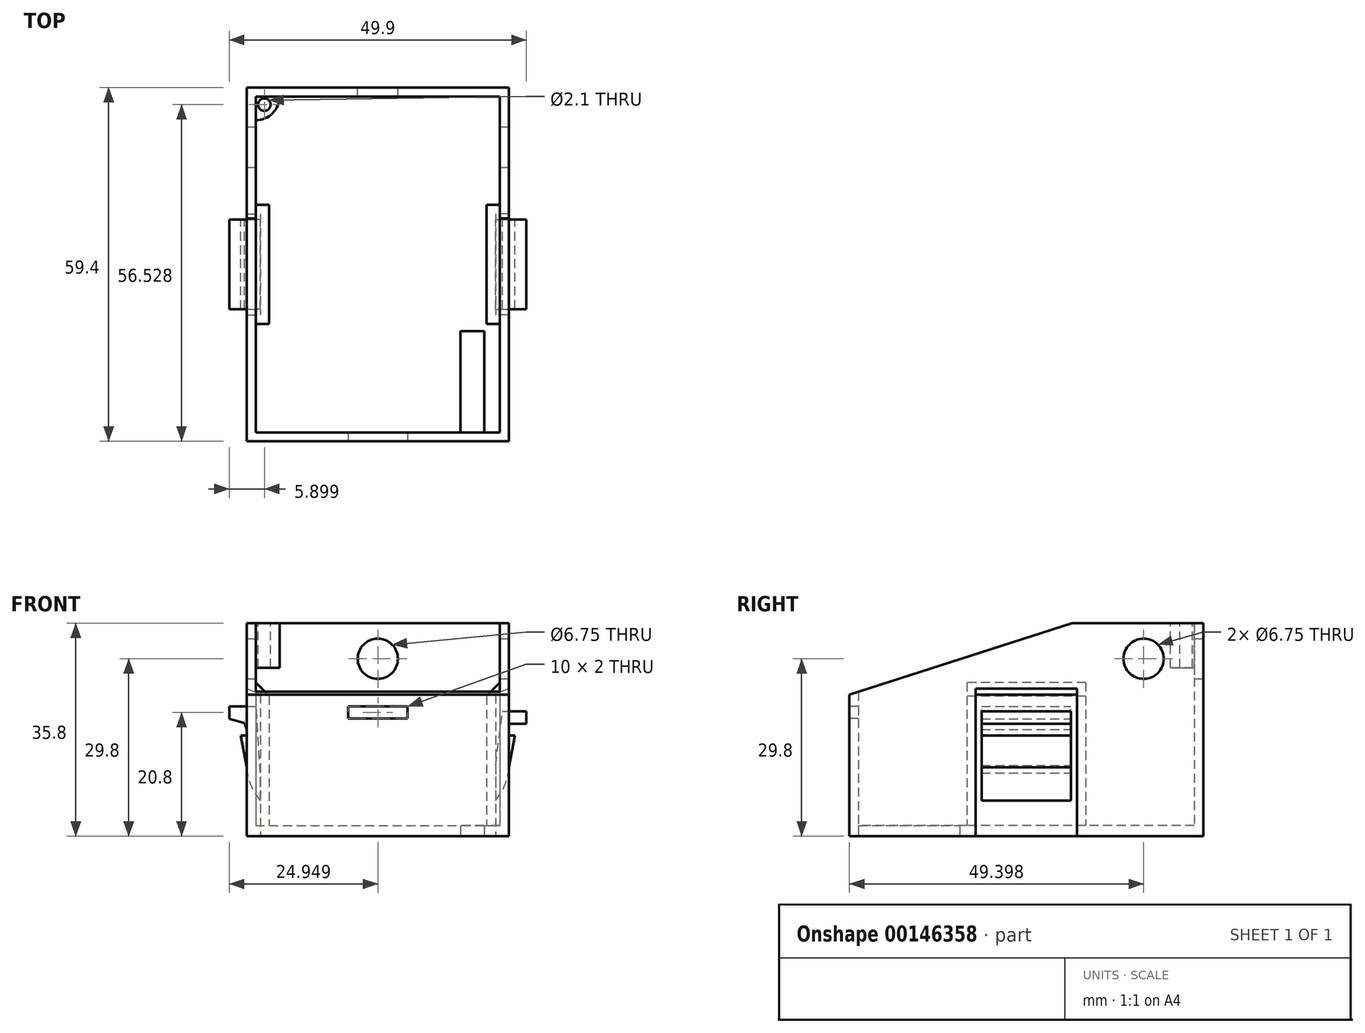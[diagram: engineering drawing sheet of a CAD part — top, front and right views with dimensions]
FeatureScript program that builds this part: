
annotation { "Feature Type Name" : "Feature", "Feature Type Description" : "" }
export const myFeature = defineFeature(function(context is Context, id is Id, definition is map)
    precondition{}
    {
        {
            var Q0;
            Q0=qCreatedBy(makeId("Top.planeOp"),FACE);
            var sketch = newSketch(context, id + "F0", { "sketchPlane" : qUnion([Q0])});
            skLineSegment(sketch, "E0.bottom", {"start": v(-56.63, 54.28) * mm, "end": v(-12.63, 54.28) * mm});
            skLineSegment(sketch, "E0.top", {"start": v(-56.63, -5.12) * mm, "end": v(-12.63, -5.12) * mm});
            skCircle(sketch, "E1", {"center": v(-12.63, -5.12) * mm, "radius": 1.5 * mm, "construction": true});
            skCircle(sketch, "E2", {"center": v(-56.63, -5.12) * mm, "radius": 1.5 * mm, "construction": true});
            skLineSegment(sketch, "E3", {"start": v(-56.63, -3.62) * mm, "end": v(-12.63, -3.62) * mm, "construction": true});
            skCircle(sketch, "E4", {"center": v(-12.63, -3.62) * mm, "radius": 4.1 * mm, "construction": true});
            skLineSegment(sketch, "E5.bottom", {"start": v(-16.73, -3.62) * mm, "end": v(-20.73, -3.62) * mm});
            skLineSegment(sketch, "E5.top", {"start": v(-16.73, 13.38) * mm, "end": v(-20.73, 13.38) * mm});
            skLineSegment(sketch, "E5.left", {"start": v(-16.73, -3.62) * mm, "end": v(-16.73, 13.38) * mm});
            skLineSegment(sketch, "E5.right", {"start": v(-20.73, -3.62) * mm, "end": v(-20.73, 13.38) * mm});
            skLineSegment(sketch, "E6", {"start": v(-56.63, 24.58) * mm, "end": v(-12.63, 24.58) * mm, "construction": true});
            skCircle(sketch, "E7", {"center": v(-56.63, 24.58) * mm, "radius": 8.5 * mm, "construction": true});
            skLineSegment(sketch, "E8", {"start": v(-56.63, 33.08) * mm, "end": v(-54.38, 33.08) * mm});
            skLineSegment(sketch, "E9", {"start": v(-56.63, 16.08) * mm, "end": v(-54.38, 16.08) * mm});
            skLineSegment(sketch, "E10", {"start": v(-54.38, 33.08) * mm, "end": v(-54.38, 16.08) * mm});
            skLineSegment(sketch, "E11", {"start": v(-56.63, 54.28) * mm, "end": v(-56.63, 33.08) * mm});
            skLineSegment(sketch, "E12", {"start": v(-56.63, 16.08) * mm, "end": v(-56.63, -5.12) * mm});
            skLineSegment(sketch, "E13", {"start": v(-34.63, 54.28) * mm, "end": v(-34.63, 40.65) * mm, "construction": true});
            skLineSegment(sketch, "E14.MirrorCS", {"start": v(-12.63, 16.08) * mm, "end": v(-12.63, -5.12) * mm});
            skLineSegment(sketch, "E15.MirrorCS", {"start": v(-12.63, 16.08) * mm, "end": v(-14.88, 16.08) * mm});
            skLineSegment(sketch, "E16.MirrorCS", {"start": v(-12.63, 33.08) * mm, "end": v(-14.88, 33.08) * mm});
            skLineSegment(sketch, "E17.MirrorCS", {"start": v(-12.63, 54.28) * mm, "end": v(-12.63, 33.08) * mm});
            skLineSegment(sketch, "E18.MirrorCS", {"start": v(-14.88, 33.08) * mm, "end": v(-14.88, 16.08) * mm});
            skSolve(sketch);
        }
        {
            var Q0;
            Q0=makeQuery(id+"F0.imprint","IMPRINT",FACE,{"disambiguationData":[TD([[makeQuery(id+"F0.imprint","IMPRINT",EDGE,{"derivedFrom":sQuery(id+"F0.wireOp",EDGE,"E0.bottom")}),-1.0]])]});
            extrude(context, id + "F1", {"entities" : qUnion([Q0]), "depth" : 1.8 * mm});
        }
        {
            var Q0;
            Q0=makeQuery(id+"F1.opExtrude","CAP_FACE",FACE,{"disambiguationData":[OSD([sQuery(id+"F0.wireOp",EDGE,"E0.bottom"),sQuery(id+"F0.wireOp",EDGE,"E0.top"),sQuery(id+"F0.wireOp",EDGE,"E5.bottom"),sQuery(id+"F0.wireOp",EDGE,"E5.top"),sQuery(id+"F0.wireOp",EDGE,"E5.left"),sQuery(id+"F0.wireOp",EDGE,"E5.right"),sQuery(id+"F0.wireOp",EDGE,"E8"),sQuery(id+"F0.wireOp",EDGE,"E9"),sQuery(id+"F0.wireOp",EDGE,"E10"),sQuery(id+"F0.wireOp",EDGE,"E11"),sQuery(id+"F0.wireOp",EDGE,"E12"),sQuery(id+"F0.wireOp",EDGE,"E14.MirrorCS"),sQuery(id+"F0.wireOp",EDGE,"E15.MirrorCS"),sQuery(id+"F0.wireOp",EDGE,"E16.MirrorCS"),sQuery(id+"F0.wireOp",EDGE,"E17.MirrorCS"),sQuery(id+"F0.wireOp",EDGE,"E18.MirrorCS")])],"isStart":false});
            var sketch = newSketch(context, id + "F2", { "sketchPlane" : qUnion([Q0])});
            skLineSegment(sketch, "E19.0", {"start": v(-55.13, 52.78) * mm, "end": v(-55.13, 34.58) * mm});
            skLineSegment(sketch, "E19.1", {"start": v(-14.13, 14.58) * mm, "end": v(-16.38, 14.58) * mm});
            skLineSegment(sketch, "E19.2", {"start": v(-16.38, 34.58) * mm, "end": v(-16.38, 14.58) * mm});
            skLineSegment(sketch, "E19.3", {"start": v(-14.13, 34.58) * mm, "end": v(-16.38, 34.58) * mm});
            skLineSegment(sketch, "E19.4", {"start": v(-14.13, 52.78) * mm, "end": v(-14.13, 34.58) * mm});
            skLineSegment(sketch, "E19.5", {"start": v(-14.13, 14.58) * mm, "end": v(-14.13, -3.62) * mm});
            skLineSegment(sketch, "E19.6", {"start": v(-55.13, 52.78) * mm, "end": v(-14.13, 52.78) * mm});
            skLineSegment(sketch, "E19.7", {"start": v(-55.13, -3.62) * mm, "end": v(-14.13, -3.62) * mm});
            skLineSegment(sketch, "E19.8", {"start": v(-55.13, 14.58) * mm, "end": v(-55.13, -3.62) * mm});
            skLineSegment(sketch, "E19.9", {"start": v(-55.13, 14.58) * mm, "end": v(-52.88, 14.58) * mm});
            skLineSegment(sketch, "E19.10", {"start": v(-52.88, 34.58) * mm, "end": v(-52.88, 14.58) * mm});
            skLineSegment(sketch, "E19.11", {"start": v(-55.13, 34.58) * mm, "end": v(-52.88, 34.58) * mm});
            skSolve(sketch);
        }
        {
            var Q0;
            Q0=makeQuery(id+"F2.imprint","IMPRINT",FACE,{"disambiguationData":[TD([[makeQuery(id+"F2.imprint","IMPRINT",EDGE,{"derivedFrom":sQuery(id+"F2.wireOp",EDGE,"E19.0")}),-1.0]])]});
            extrude(context, id + "F3", {"entities" : qUnion([Q0]), "operationType" : NewBodyOperationType.ADD, "depth" : 22 * mm});
        }
        {
            var Q0;
            Q0=makeQuery(id+"F3.opExtrude","CAP_FACE",FACE,{"disambiguationData":[OSD([sQuery(id+"F0.wireOp",EDGE,"E0.bottom"),sQuery(id+"F0.wireOp",EDGE,"E0.top"),sQuery(id+"F0.wireOp",EDGE,"E8"),sQuery(id+"F0.wireOp",EDGE,"E9"),sQuery(id+"F0.wireOp",EDGE,"E10"),sQuery(id+"F0.wireOp",EDGE,"E11"),sQuery(id+"F0.wireOp",EDGE,"E12"),sQuery(id+"F0.wireOp",EDGE,"E14.MirrorCS"),sQuery(id+"F0.wireOp",EDGE,"E15.MirrorCS"),sQuery(id+"F0.wireOp",EDGE,"E16.MirrorCS"),sQuery(id+"F0.wireOp",EDGE,"E17.MirrorCS"),sQuery(id+"F0.wireOp",EDGE,"E18.MirrorCS"),sQuery(id+"F2.wireOp",EDGE,"E19.0"),sQuery(id+"F2.wireOp",EDGE,"E19.1"),sQuery(id+"F2.wireOp",EDGE,"E19.2"),sQuery(id+"F2.wireOp",EDGE,"E19.3"),sQuery(id+"F2.wireOp",EDGE,"E19.4"),sQuery(id+"F2.wireOp",EDGE,"E19.5"),sQuery(id+"F2.wireOp",EDGE,"E19.6"),sQuery(id+"F2.wireOp",EDGE,"E19.7"),sQuery(id+"F2.wireOp",EDGE,"E19.8"),sQuery(id+"F2.wireOp",EDGE,"E19.9"),sQuery(id+"F2.wireOp",EDGE,"E19.10"),sQuery(id+"F2.wireOp",EDGE,"E19.11")])],"isStart":false});
            var sketch = newSketch(context, id + "F4", { "sketchPlane" : qUnion([Q0])});
            skLineSegment(sketch, "E20.bottom", {"start": v(-56.63, 54.28) * mm, "end": v(-12.63, 54.28) * mm});
            skLineSegment(sketch, "E20.top", {"start": v(-56.63, -5.12) * mm, "end": v(-12.63, -5.12) * mm});
            skLineSegment(sketch, "E20.left", {"start": v(-56.63, 54.28) * mm, "end": v(-56.63, -5.12) * mm});
            skLineSegment(sketch, "E20.right", {"start": v(-12.63, 54.28) * mm, "end": v(-12.63, -5.12) * mm});
            skLineSegment(sketch, "E21.bottom", {"start": v(-55.13, 52.78) * mm, "end": v(-14.13, 52.78) * mm});
            skLineSegment(sketch, "E21.top", {"start": v(-55.13, -3.62) * mm, "end": v(-14.13, -3.62) * mm});
            skLineSegment(sketch, "E22", {"start": v(-14.13, 52.78) * mm, "end": v(-55.13, 52.78) * mm});
            skLineSegment(sketch, "E23", {"start": v(-55.13, 52.78) * mm, "end": v(-55.13, 34.58) * mm});
            skLineSegment(sketch, "E24", {"start": v(-55.13, 34.58) * mm, "end": v(-52.88, 34.58) * mm});
            skLineSegment(sketch, "E25", {"start": v(-52.88, 34.58) * mm, "end": v(-52.88, 14.58) * mm});
            skLineSegment(sketch, "E26", {"start": v(-52.88, 14.58) * mm, "end": v(-55.13, 14.58) * mm});
            skLineSegment(sketch, "E27", {"start": v(-55.13, 14.58) * mm, "end": v(-55.13, -3.62) * mm});
            skLineSegment(sketch, "E28", {"start": v(-14.13, -3.62) * mm, "end": v(-14.13, 14.58) * mm});
            skLineSegment(sketch, "E29", {"start": v(-14.13, 14.58) * mm, "end": v(-16.38, 14.58) * mm});
            skLineSegment(sketch, "E30", {"start": v(-16.38, 14.58) * mm, "end": v(-16.38, 34.58) * mm});
            skLineSegment(sketch, "E31", {"start": v(-16.38, 34.58) * mm, "end": v(-14.13, 34.58) * mm});
            skLineSegment(sketch, "E32", {"start": v(-14.13, 34.58) * mm, "end": v(-14.13, 52.78) * mm});
            skSolve(sketch);
        }
        {
            var Q0;
            Q0=qSketchRegion(id+"F4",true);
            extrude(context, id + "F5", {"entities" : qUnion([Q0]), "operationType" : NewBodyOperationType.ADD, "depth" : 12 * mm});
        }
        {
            var Q0;
            Q0=makeQuery(id+"F5.opExtrude","CAP_FACE",FACE,{"disambiguationData":[OSD([sQuery(id+"F4.wireOp",EDGE,"E20.bottom"),sQuery(id+"F4.wireOp",EDGE,"E20.top"),sQuery(id+"F4.wireOp",EDGE,"E20.left"),sQuery(id+"F4.wireOp",EDGE,"E20.right"),sQuery(id+"F4.wireOp",EDGE,"E21.top"),sQuery(id+"F4.wireOp",EDGE,"E22"),sQuery(id+"F4.wireOp",EDGE,"E23"),sQuery(id+"F4.wireOp",EDGE,"E24"),sQuery(id+"F4.wireOp",EDGE,"E25"),sQuery(id+"F4.wireOp",EDGE,"E26"),sQuery(id+"F4.wireOp",EDGE,"E27"),sQuery(id+"F4.wireOp",EDGE,"E28"),sQuery(id+"F4.wireOp",EDGE,"E29"),sQuery(id+"F4.wireOp",EDGE,"E30"),sQuery(id+"F4.wireOp",EDGE,"E31"),sQuery(id+"F4.wireOp",EDGE,"E32")])],"isStart":false});
            var sketch = newSketch(context, id + "F6", { "sketchPlane" : qUnion([Q0])});
            skLineSegment(sketch, "E33.bottom", {"start": v(-55.13, 34.58) * mm, "end": v(-52.88, 34.58) * mm});
            skLineSegment(sketch, "E33.top", {"start": v(-55.13, 14.58) * mm, "end": v(-52.88, 14.58) * mm});
            skLineSegment(sketch, "E33.left", {"start": v(-55.13, 34.58) * mm, "end": v(-55.13, 14.58) * mm});
            skLineSegment(sketch, "E33.right", {"start": v(-52.88, 34.58) * mm, "end": v(-52.88, 14.58) * mm});
            skLineSegment(sketch, "E34.bottom", {"start": v(-16.38, 34.58) * mm, "end": v(-14.13, 34.58) * mm});
            skLineSegment(sketch, "E34.top", {"start": v(-16.38, 14.58) * mm, "end": v(-14.13, 14.58) * mm});
            skLineSegment(sketch, "E34.left", {"start": v(-16.38, 34.58) * mm, "end": v(-16.38, 14.58) * mm});
            skLineSegment(sketch, "E34.right", {"start": v(-14.13, 34.58) * mm, "end": v(-14.13, 14.58) * mm});
            skSolve(sketch);
        }
        {
            var Q0;
            Q0=qSketchRegion(id+"F6",true);
            extrude(context, id + "F7", {"entities" : qUnion([Q0]), "operationType" : NewBodyOperationType.REMOVE, "oppositeDirection" : true, "depth" : 10 * mm});
        }
        {
            var Q0;
            Q0=makeQuery(id+"F5.boolean.opBoolean","MERGE",FACE,{"derivedFrom":[makeQuery(id+"F3.opExtrude","SWEPT_FACE",FACE,{"disambiguationData":[OSD([sQuery(id+"F2.wireOp",EDGE,"E19.9")])]}),makeQuery(id+"F5.opExtrude","SWEPT_FACE",FACE,{"disambiguationData":[OSD([sQuery(id+"F4.wireOp",EDGE,"E26")])]})]});
            var sketch = newSketch(context, id + "F8", { "sketchPlane" : qUnion([Q0])});
            skLineSegment(sketch, "E35", {"start": v(-55.13, 25.8) * mm, "end": v(-52.88, 23.55) * mm});
            skLineSegment(sketch, "E36", {"start": v(-52.88, 23.55) * mm, "end": v(-52.88, 25.8) * mm});
            skLineSegment(sketch, "E37", {"start": v(-52.88, 25.8) * mm, "end": v(-55.13, 25.8) * mm});
            skSolve(sketch);
        }
        {
            var Q0;
            Q0=makeQuery(id+"F8.imprint","IMPRINT",FACE,{"disambiguationData":[TD([[makeQuery(id+"F8.imprint","IMPRINT",EDGE,{"derivedFrom":sQuery(id+"F8.wireOp",EDGE,"E35")}),1.0]])]});
            extrude(context, id + "F9", {"entities" : qUnion([Q0]), "operationType" : NewBodyOperationType.REMOVE, "oppositeDirection" : true, "depth" : 20 * mm});
        }
        {
            var Q0;
            {var subQ0=sQuery(id+"F0.wireOp",EDGE,"E8");Q0=makeQuery(id+"F3.boolean.opBoolean","MERGE",FACE,{"derivedFrom":[makeQuery(id+"F1.opExtrude","SWEPT_FACE",FACE,{"disambiguationData":[OSD([subQ0])]}),makeQuery(id+"F3.opExtrude","SWEPT_FACE",FACE,{"disambiguationData":[OSD([subQ0])]})]});}
            var sketch = newSketch(context, id + "F10", { "sketchPlane" : qUnion([Q0])});
            skLineSegment(sketch, "E38", {"start": v(-56.63, 23.8) * mm, "end": v(-54.38, 23.8) * mm});
            skLineSegment(sketch, "E39", {"start": v(-56.63, 23.8) * mm, "end": v(-56.63, 24.8) * mm});
            skLineSegment(sketch, "E40", {"start": v(-56.63, 23.8) * mm, "end": v(-55.5, 23.8) * mm});
            skCircle(sketch, "E41", {"center": v(-56.63, 23.8) * mm, "radius": 2 * mm, "construction": true});
            skLineSegment(sketch, "E42", {"start": v(-56.63, 24.8) * mm, "end": v(-54.38, 23.8) * mm});
            skSolve(sketch);
        }
        {
            var Q0;
            Q0=qSketchRegion(id+"F10",true);
            extrude(context, id + "F11", {"entities" : qUnion([Q0]), "operationType" : NewBodyOperationType.REMOVE, "depth" : 17 * mm});
        }
        {
            var Q0;
            Q0=makeQuery(id+"F5.boolean.opBoolean","MERGE",FACE,{"derivedFrom":[makeQuery(id+"F3.opExtrude","SWEPT_FACE",FACE,{"disambiguationData":[OSD([sQuery(id+"F2.wireOp",EDGE,"E19.3")])]}),makeQuery(id+"F5.opExtrude","SWEPT_FACE",FACE,{"disambiguationData":[OSD([sQuery(id+"F4.wireOp",EDGE,"E31")])]})]});
            var sketch = newSketch(context, id + "F12", { "sketchPlane" : qUnion([Q0])});
            skLineSegment(sketch, "E43", {"start": v(16.38, 25.8) * mm, "end": v(14.13, 25.8) * mm});
            skLineSegment(sketch, "E44", {"start": v(14.13, 25.8) * mm, "end": v(16.38, 23.55) * mm});
            skLineSegment(sketch, "E45", {"start": v(16.38, 23.55) * mm, "end": v(16.38, 25.8) * mm});
            skSolve(sketch);
        }
        {
            var Q0;
            Q0=qSketchRegion(id+"F12",true);
            extrude(context, id + "F13", {"entities" : qUnion([Q0]), "operationType" : NewBodyOperationType.REMOVE, "oppositeDirection" : true, "depth" : 20 * mm});
        }
        {
            var Q0;
            {var subQ0=sQuery(id+"F0.wireOp",EDGE,"E15.MirrorCS");Q0=makeQuery(id+"F3.boolean.opBoolean","MERGE",FACE,{"derivedFrom":[makeQuery(id+"F1.opExtrude","SWEPT_FACE",FACE,{"disambiguationData":[OSD([subQ0])]}),makeQuery(id+"F3.opExtrude","SWEPT_FACE",FACE,{"disambiguationData":[OSD([subQ0])]})]});}
            var sketch = newSketch(context, id + "F14", { "sketchPlane" : qUnion([Q0])});
            skLineSegment(sketch, "E46", {"start": v(12.63, 23.8) * mm, "end": v(12.63, 24.8) * mm});
            skLineSegment(sketch, "E47", {"start": v(12.63, 24.8) * mm, "end": v(14.88, 23.8) * mm});
            skLineSegment(sketch, "E48", {"start": v(14.88, 23.8) * mm, "end": v(12.63, 23.8) * mm});
            skSolve(sketch);
        }
        {
            var Q0;
            Q0=qSketchRegion(id+"F14",true);
            extrude(context, id + "F15", {"entities" : qUnion([Q0]), "operationType" : NewBodyOperationType.REMOVE, "depth" : 17 * mm});
        }
        {
            var Q0;
            {var subQ0=sQuery(id+"F0.wireOp",EDGE,"E17.MirrorCS");var subQ1=sQuery(id+"F0.wireOp",EDGE,"E14.MirrorCS");Q0=makeQuery(id+"F5.boolean.opBoolean","MERGE",FACE,{"derivedFrom":[makeQuery(id+"F3.boolean.opBoolean","MERGE",FACE,{"derivedFrom":[makeQuery(id+"F1.opExtrude","SWEPT_FACE",FACE,{"disambiguationData":[OSD([subQ1])]}),makeQuery(id+"F3.opExtrude","SWEPT_FACE",FACE,{"disambiguationData":[OSD([subQ1])]})]}),makeQuery(id+"F3.boolean.opBoolean","MERGE",FACE,{"derivedFrom":[makeQuery(id+"F1.opExtrude","SWEPT_FACE",FACE,{"disambiguationData":[OSD([subQ0])]}),makeQuery(id+"F3.opExtrude","SWEPT_FACE",FACE,{"disambiguationData":[OSD([subQ0])]})]}),makeQuery(id+"F5.opExtrude","SWEPT_FACE",FACE,{"disambiguationData":[OSD([sQuery(id+"F4.wireOp",EDGE,"E20.right")])]})]});}
            var sketch = newSketch(context, id + "F16", { "sketchPlane" : qUnion([Q0])});
            skCircle(sketch, "E49", {"center": v(-5.12, 35.8) * mm, "radius": 12 * mm, "construction": true});
            skCircle(sketch, "E50", {"center": v(54.28, 35.8) * mm, "radius": 22 * mm, "construction": true});
            skLineSegment(sketch, "E51", {"start": v(-5.12, 35.8) * mm, "end": v(-5.12, 23.8) * mm});
            skLineSegment(sketch, "E52", {"start": v(-5.12, 23.8) * mm, "end": v(32.28, 35.8) * mm});
            skLineSegment(sketch, "E53", {"start": v(32.28, 35.8) * mm, "end": v(-5.12, 35.8) * mm});
            skCircle(sketch, "E54", {"center": v(54.28, 35.8) * mm, "radius": 10 * mm, "construction": true});
            skLineSegment(sketch, "E55", {"start": v(44.28, 35.8) * mm, "end": v(44.28, 29.8) * mm, "construction": true});
            skCircle(sketch, "E56", {"center": v(44.28, 29.8) * mm, "radius": 3.38 * mm});
            skSolve(sketch);
        }
        {
            var Q0;
            Q0=qSketchRegion(id+"F16",true);
            extrude(context, id + "F17", {"entities" : qUnion([Q0]), "operationType" : NewBodyOperationType.REMOVE, "oppositeDirection" : true, "depth" : 45 * mm});
        }
        {
            var Q0;
            {var subQ0=sQuery(id+"F0.wireOp",EDGE,"E0.bottom");Q0=makeQuery(id+"F5.boolean.opBoolean","MERGE",FACE,{"derivedFrom":[makeQuery(id+"F3.boolean.opBoolean","MERGE",FACE,{"derivedFrom":[makeQuery(id+"F1.opExtrude","SWEPT_FACE",FACE,{"disambiguationData":[OSD([subQ0])]}),makeQuery(id+"F3.opExtrude","SWEPT_FACE",FACE,{"disambiguationData":[OSD([subQ0])]})]}),makeQuery(id+"F5.opExtrude","SWEPT_FACE",FACE,{"disambiguationData":[OSD([sQuery(id+"F4.wireOp",EDGE,"E20.bottom")])]})]});}
            var sketch = newSketch(context, id + "F18", { "sketchPlane" : qUnion([Q0])});
            skLineSegment(sketch, "E57", {"start": v(34.63, 35.8) * mm, "end": v(34.63, 29.8) * mm, "construction": true});
            skCircle(sketch, "E58", {"center": v(34.63, 29.8) * mm, "radius": 3.38 * mm});
            skSolve(sketch);
        }
        {
            var Q0;
            Q0=qSketchRegion(id+"F18",true);
            extrude(context, id + "F19", {"entities" : qUnion([Q0]), "operationType" : NewBodyOperationType.REMOVE, "oppositeDirection" : true, "depth" : 3 * mm});
        }
        {
            var Q0;
            Q0=makeQuery(id+"F5.opExtrude","CAP_FACE",FACE,{"disambiguationData":[OSD([sQuery(id+"F4.wireOp",EDGE,"E20.bottom"),sQuery(id+"F4.wireOp",EDGE,"E20.top"),sQuery(id+"F4.wireOp",EDGE,"E20.left"),sQuery(id+"F4.wireOp",EDGE,"E20.right"),sQuery(id+"F4.wireOp",EDGE,"E21.top"),sQuery(id+"F4.wireOp",EDGE,"E22"),sQuery(id+"F4.wireOp",EDGE,"E23"),sQuery(id+"F4.wireOp",EDGE,"E24"),sQuery(id+"F4.wireOp",EDGE,"E25"),sQuery(id+"F4.wireOp",EDGE,"E26"),sQuery(id+"F4.wireOp",EDGE,"E27"),sQuery(id+"F4.wireOp",EDGE,"E28"),sQuery(id+"F4.wireOp",EDGE,"E29"),sQuery(id+"F4.wireOp",EDGE,"E30"),sQuery(id+"F4.wireOp",EDGE,"E31"),sQuery(id+"F4.wireOp",EDGE,"E32")])],"isStart":false});
            var sketch = newSketch(context, id + "F20", { "sketchPlane" : qUnion([Q0])});
            skArc(sketch, "E59", {"start": v(-55.13, 48.78) * mm, "mid": v(-52.3, 49.96) * mm, "end": v(-51.13, 52.78) * mm});
            skLineSegment(sketch, "E60", {"start": v(-55.13, 52.78) * mm, "end": v(-52.23, 50.04) * mm, "construction": true});
            skLineSegment(sketch, "E61", {"start": v(-34.63, 54.28) * mm, "end": v(-34.63, 59.78) * mm, "construction": true});
            skCircle(sketch, "E62", {"center": v(-53.68, 51.4) * mm, "radius": 1.05 * mm});
            skArc(sketch, "E63.MirrorCS", {"start": v(-14.13, 48.78) * mm, "mid": v(-16.95, 49.96) * mm, "end": v(-18.13, 52.78) * mm});
            skCircle(sketch, "E64.MirrorC", {"center": v(-15.58, 51.4) * mm, "radius": 1.05 * mm});
            skSolve(sketch);
        }
        {
            var Q0;
            {var subQ0=sQuery(id+"F20.wireOp",EDGE,"E59");Q0=makeQuery(id+"F20.imprint","IMPRINT",FACE,{"disambiguationData":[TD([[makeQuery(id+"F20.imprint","IMPRINT",EDGE,{"derivedFrom":subQ0}),1.0]])]});}
            var Q1;
            {var subQ0=sQuery(id+"F20.wireOp",EDGE,"E63.MirrorCS");Q1=makeQuery(id+"F20.imprint","IMPRINT",FACE,{"disambiguationData":[TD([[makeQuery(id+"F20.imprint","IMPRINT",EDGE,{"derivedFrom":subQ0}),-1.0]])]});}
            extrude(context, id + "F21", {"entities" : qUnion([Q0, Q1]), "oppositeDirection" : true, "depth" : 7.5 * mm});
        }
        {
            var Q0;
            {var subQ0=sQuery(id+"F0.wireOp",EDGE,"E0.top");Q0=makeQuery(id+"F5.boolean.opBoolean","MERGE",FACE,{"derivedFrom":[makeQuery(id+"F3.boolean.opBoolean","MERGE",FACE,{"derivedFrom":[makeQuery(id+"F1.opExtrude","SWEPT_FACE",FACE,{"disambiguationData":[OSD([subQ0])]}),makeQuery(id+"F3.opExtrude","SWEPT_FACE",FACE,{"disambiguationData":[OSD([subQ0])]})]}),makeQuery(id+"F5.opExtrude","SWEPT_FACE",FACE,{"disambiguationData":[OSD([sQuery(id+"F4.wireOp",EDGE,"E20.top")])]})]});}
            var sketch = newSketch(context, id + "F22", { "sketchPlane" : qUnion([Q0])});
            skCircle(sketch, "E65", {"center": v(-56.63, 23.8) * mm, "radius": 2 * mm, "construction": true});
            skLineSegment(sketch, "E66", {"start": v(-56.63, 21.8) * mm, "end": v(-12.63, 21.8) * mm, "construction": true});
            skCircle(sketch, "E67", {"center": v(-34.63, 21.8) * mm, "radius": 5 * mm, "construction": true});
            skLineSegment(sketch, "E68", {"start": v(-29.63, 21.8) * mm, "end": v(-29.63, 19.8) * mm});
            skLineSegment(sketch, "E69.bottom", {"start": v(-29.63, 19.8) * mm, "end": v(-39.63, 19.8) * mm});
            skLineSegment(sketch, "E69.top", {"start": v(-29.63, 21.8) * mm, "end": v(-39.63, 21.8) * mm});
            skLineSegment(sketch, "E69.left", {"start": v(-29.63, 19.8) * mm, "end": v(-29.63, 21.8) * mm});
            skLineSegment(sketch, "E69.right", {"start": v(-39.63, 19.8) * mm, "end": v(-39.63, 21.8) * mm});
            skSolve(sketch);
        }
        {
            var Q0;
            Q0=qSketchRegion(id+"F22",true);
            extrude(context, id + "F23", {"entities" : qUnion([Q0]), "operationType" : NewBodyOperationType.REMOVE, "oppositeDirection" : true, "depth" : 2.5 * mm});
        }
        {
            var Q0;
            {var subQ0=sQuery(id+"F0.wireOp",EDGE,"E16.MirrorCS");Q0=makeQuery(id+"F15.boolean.opBoolean","MERGE",FACE,{"derivedFrom":[makeQuery(id+"F3.boolean.opBoolean","MERGE",FACE,{"derivedFrom":[makeQuery(id+"F1.opExtrude","SWEPT_FACE",FACE,{"disambiguationData":[OSD([subQ0])]}),makeQuery(id+"F3.opExtrude","SWEPT_FACE",FACE,{"disambiguationData":[OSD([subQ0])]})]}),makeQuery(id+"F15.opExtrude","CAP_FACE",FACE,{"disambiguationData":[OSD([sQuery(id+"F14.wireOp",EDGE,"E46"),sQuery(id+"F14.wireOp",EDGE,"E47"),sQuery(id+"F14.wireOp",EDGE,"E48")])],"isStart":false})]});}
            var sketch = newSketch(context, id + "F24", { "sketchPlane" : qUnion([Q0])});
            skLineSegment(sketch, "E70", {"start": v(-14.88, 0) * mm, "end": v(-14.88, 6) * mm, "construction": true});
            skCircle(sketch, "E71", {"center": v(-14.88, 6) * mm, "radius": 6 * mm, "construction": true});
            skArc(sketch, "E72", {"start": v(-14.88, 6) * mm, "mid": v(-13.3, 8.6) * mm, "end": v(-12.63, 11.56) * mm});
            skCircle(sketch, "E73", {"center": v(-14.88, 11.9) * mm, "radius": 5 * mm, "construction": true});
            skLineSegment(sketch, "E74", {"start": v(-14.88, 16.9) * mm, "end": v(-5.95, 16.9) * mm, "construction": true});
            skCircle(sketch, "E75", {"center": v(-12.63, 16.9) * mm, "radius": 1 * mm, "construction": true});
            skLineSegment(sketch, "E76", {"start": v(-12.63, 11.56) * mm, "end": v(-11.63, 16.9) * mm});
            skCircle(sketch, "E77", {"center": v(-14.88, 16.9) * mm, "radius": 1.2 * mm, "construction": true});
            skLineSegment(sketch, "E78", {"start": v(-13.68, 21) * mm, "end": v(-9.68, 21) * mm});
            skLineSegment(sketch, "E79", {"start": v(-11.63, 16.9) * mm, "end": v(-12.63, 16.9) * mm});
            skCircle(sketch, "E80", {"center": v(-12.63, 16.9) * mm, "radius": 2 * mm, "construction": true});
            skLineSegment(sketch, "E81", {"start": v(-12.63, 16.9) * mm, "end": v(-12.63, 18.9) * mm});
            skLineSegment(sketch, "E82", {"start": v(-12.63, 18.9) * mm, "end": v(-9.68, 18.9) * mm});
            skLineSegment(sketch, "E83", {"start": v(-14.88, 11.9) * mm, "end": v(-13.68, 21) * mm});
            skLineSegment(sketch, "E84", {"start": v(-9.68, 21) * mm, "end": v(-9.68, 18.9) * mm});
            skLineSegment(sketch, "E85", {"start": v(-12.63, 6.02) * mm, "end": v(-56.63, 6.02) * mm, "construction": true});
            skLineSegment(sketch, "E86", {"start": v(-34.63, 6.02) * mm, "end": v(-34.63, 12.32) * mm, "construction": true});
            skCircle(sketch, "E87.MirrorC", {"center": v(-56.63, 16.9) * mm, "radius": 2 * mm, "construction": true});
            skLineSegment(sketch, "E88.MirrorCS", {"start": v(-56.63, 11.56) * mm, "end": v(-57.63, 16.9) * mm});
            skArc(sketch, "E89.MirrorCS", {"start": v(-54.38, 6) * mm, "mid": v(-55.96, 8.6) * mm, "end": v(-56.63, 11.56) * mm});
            skLineSegment(sketch, "E90.MirrorCS", {"start": v(-57.63, 16.9) * mm, "end": v(-56.63, 16.9) * mm});
            skLineSegment(sketch, "E91", {"start": v(-14.88, 11.9) * mm, "end": v(-14.88, 6) * mm});
            skCircle(sketch, "E92", {"center": v(-56.63, 18.9) * mm, "radius": 0.8 * mm, "construction": true});
            skPoint(sketch, "E93.endSnap0", {"position": v(-56.63, 17.9) * mm});
            skLineSegment(sketch, "E94", {"start": v(-56.63, 19.7) * mm, "end": v(-59.88, 19.7) * mm, "construction": true});
            skLineSegment(sketch, "E95", {"start": v(-59.58, 19.7) * mm, "end": v(-59.58, 21.8) * mm});
            skLineSegment(sketch, "E96", {"start": v(-59.58, 19.7) * mm, "end": v(-57.03, 19) * mm});
            skLineSegment(sketch, "E97", {"start": v(-56.63, 16.9) * mm, "end": v(-56.63, 17.9) * mm});
            skLineSegment(sketch, "E98", {"start": v(-56.63, 17.9) * mm, "end": v(-57.03, 19) * mm});
            skLineSegment(sketch, "E99", {"start": v(-59.58, 21.8) * mm, "end": v(-55.04, 21.8) * mm});
            skLineSegment(sketch, "E100", {"start": v(-54.38, 6) * mm, "end": v(-54.38, 10.6) * mm});
            skLineSegment(sketch, "E101", {"start": v(-54.38, 10.6) * mm, "end": v(-55.04, 21.8) * mm});
            skSolve(sketch);
        }
        {
            var Q0;
            Q0=makeQuery(id+"F24.imprint","IMPRINT",FACE,{"disambiguationData":[TD([[makeQuery(id+"F24.imprint","IMPRINT",EDGE,{"derivedFrom":sQuery(id+"F24.wireOp",EDGE,"3a5f83b2-c532-4f29-86cb-ad45a0fee2c30.MirrorCS")}),1.0]])]});
            var Q1;
            {var subQ6=sQuery(id+"F24.wireOp",EDGE,"E82");Q1=makeQuery(id+"F24.imprint","IMPRINT",FACE,{"disambiguationData":[TD([[makeQuery(id+"F24.imprint","IMPRINT",EDGE,{"derivedFrom":subQ6}),1.0]])]});}
            var Q2;
            {var subQ7=sQuery(id+"F24.wireOp",EDGE,"E72");Q2=makeQuery(id+"F24.imprint","IMPRINT",FACE,{"disambiguationData":[TD([[makeQuery(id+"F24.imprint","IMPRINT",EDGE,{"derivedFrom":subQ7}),1.0]])]});}
            var Q3;
            {var subQ0=sQuery(id+"F24.wireOp",EDGE,"E76");Q3=makeQuery(id+"F24.imprint","IMPRINT",FACE,{"disambiguationData":[TD([[makeQuery(id+"F24.imprint","IMPRINT",EDGE,{"derivedFrom":subQ0}),1.0]])]});}
            var Q4;
            Q4=makeQuery(id+"F24.imprint","IMPRINT",FACE,{"disambiguationData":[TD([[makeQuery(id+"F24.imprint","IMPRINT",EDGE,{"derivedFrom":sQuery(id+"F24.wireOp",EDGE,"E88.MirrorCS")}),-1.0]])]});
            extrude(context, id + "F25", {"entities" : qUnion([Q0, Q1, Q2, Q3, Q4]), "operationType" : NewBodyOperationType.ADD, "depth" : 16 * mm, "hasSecondDirection" : true, "secondDirectionOppositeDirection" : false, "secondDirectionDepth" : 1 * mm});
        }
    });
